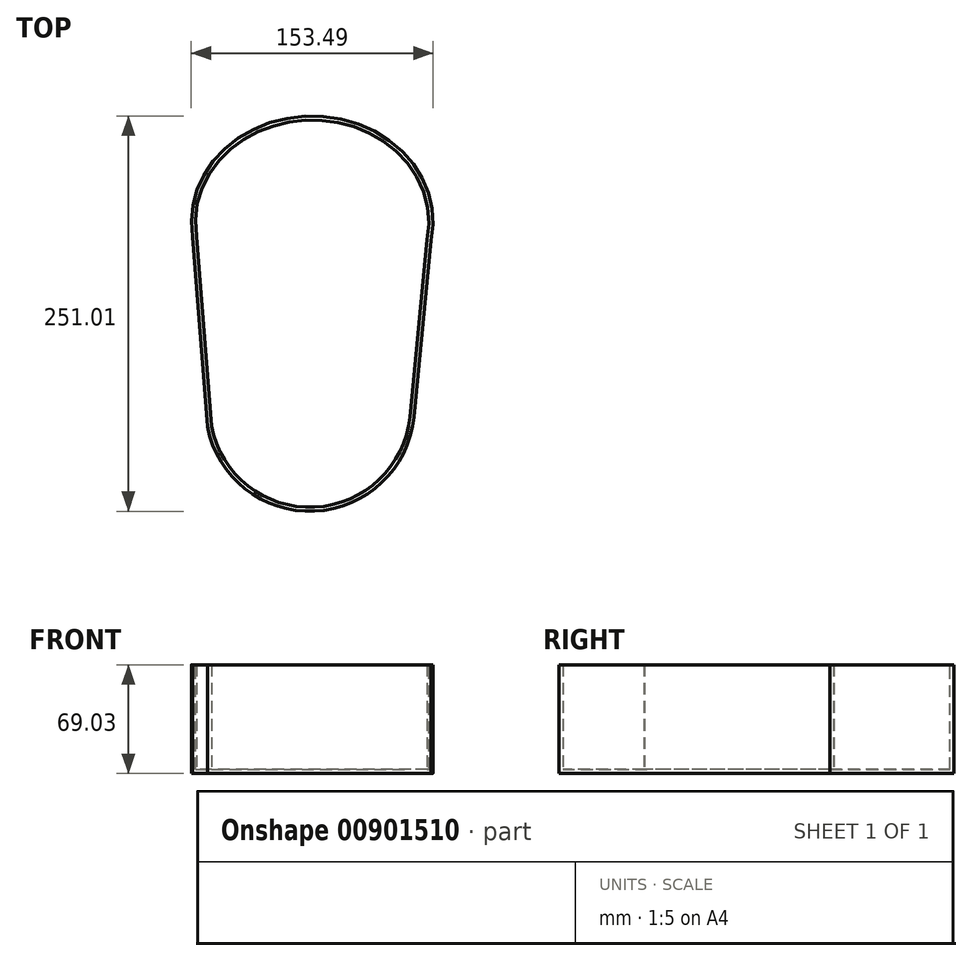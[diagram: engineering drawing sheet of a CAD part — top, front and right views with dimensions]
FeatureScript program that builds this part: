
annotation { "Feature Type Name" : "Feature", "Feature Type Description" : "" }
export const myFeature = defineFeature(function(context is Context, id is Id, definition is map)
    precondition{}
    {
        {
            var Q0;
            Q0=qCreatedBy(makeId("Top.planeOp"),FACE);
            var sketch = newSketch(context, id + "F0", { "sketchPlane" : qUnion([Q0])});
            skEllipse(sketch, "E0", {"center": v(54.44, 50.32) * mm, "majorRadius": 76.74 * mm, "minorRadius": 67.38 * mm, "majorAxis": v(1, 0)});
            skLineSegment(sketch, "E1", {"start": v(-22.3, 50.32) * mm, "end": v(-12.04, -79.46) * mm});
            skLineSegment(sketch, "E2", {"start": v(131.18, 50.32) * mm, "end": v(119, -73.53) * mm});
            skArc(sketch, "E3", {"start": v(-12.04, -79.46) * mm, "mid": v(56.05, -133.24) * mm, "end": v(119, -73.53) * mm});
            skSolve(sketch);
        }
        {
            var Q0;
            Q0 = qSketchRegion(id + "F0", true);
            extrude(context, id + "F1", {"entities" : qUnion([Q0]), "depth" : 69.03 * mm, "offsetDistance" : 25.4 * mm});
        }
        {
            var Q0;
            Q0=makeQuery(id+"F1.opExtrude","CAP_FACE",FACE,{"disambiguationData":[OSD([sQuery(id+"F0.wireOp",EDGE,"E0"),sQuery(id+"F0.wireOp",EDGE,"E1"),sQuery(id+"F0.wireOp",EDGE,"E2"),sQuery(id+"F0.wireOp",EDGE,"E3")])],"isStart":false});
            var sketch = newSketch(context, id + "F2", { "sketchPlane" : qUnion([Q0])});
            skCircle(sketch, "E4", {"center": v(54.44, 50.32) * mm, "radius": 36.07 * mm});
            skCircle(sketch, "E5", {"center": v(50.75, -88.6) * mm, "radius": 32.82 * mm});
            skSolve(sketch);
        }
        {
            var Q0;
            Q0=sQuery(id+"F2.wireOp",EDGE,"E4");
            var Q1;
            Q1=sQuery(id+"F2.wireOp",EDGE,"E5");
            var Q2;
            Q2 = qBodyType(qCreatedBy(id + "F2" ,EDGE), BodyType.WIRE);
            extrude(context, id + "F3", {"bodyType" : ToolBodyType.SURFACE, "surfaceEntities" : qUnion([Q0, Q1, Q2]), "depth" : 54.4 * mm, "offsetDistance" : 25.4 * mm});
        }
        {
            var Q0;
            Q0=makeQuery(id+"F1.opExtrude","CAP_FACE",FACE,{"disambiguationData":[OSD([sQuery(id+"F0.wireOp",EDGE,"E0"),sQuery(id+"F0.wireOp",EDGE,"E1"),sQuery(id+"F0.wireOp",EDGE,"E2"),sQuery(id+"F0.wireOp",EDGE,"E3")])],"isStart":false});
            shell(context, id + "F4", {"entities" : qUnion([Q0]), "thickness" : 2.54 * mm});
        }
    });
